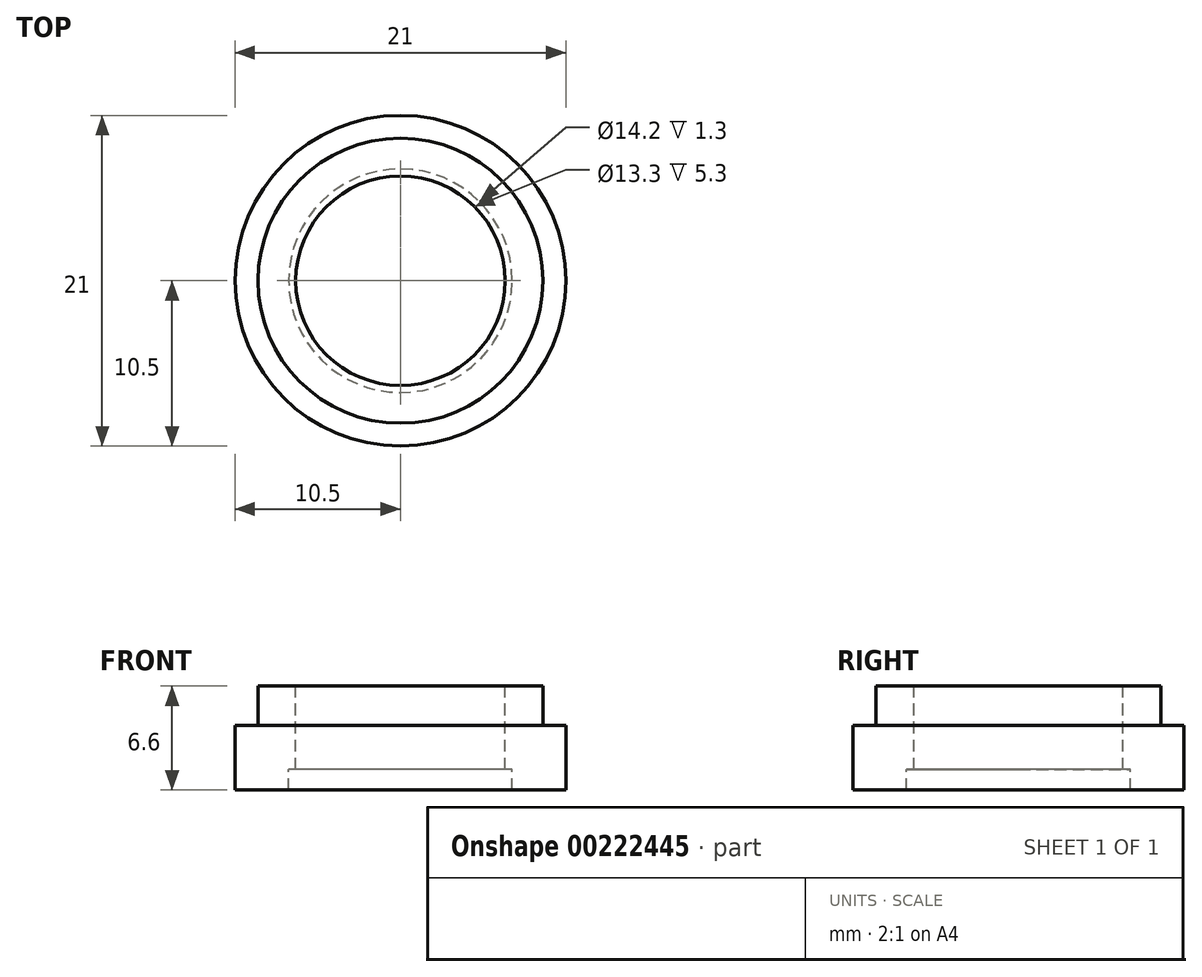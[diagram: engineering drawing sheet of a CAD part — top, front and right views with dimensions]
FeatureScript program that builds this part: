
annotation { "Feature Type Name" : "Feature", "Feature Type Description" : "" }
export const myFeature = defineFeature(function(context is Context, id is Id, definition is map)
    precondition{}
    {
        {
            var Q0;
            Q0=qCreatedBy(makeId("Front.planeOp"),FACE);
            var sketch = newSketch(context, id + "F0", { "sketchPlane" : qUnion([Q0])});
            skLineSegment(sketch, "E0", {"start": v(0, 26.98) * mm, "end": v(0, -14) * mm, "construction": true});
            skLineSegment(sketch, "E1", {"start": v(-7.1, 14.04) * mm, "end": v(-10.5, 14.04) * mm});
            skLineSegment(sketch, "E2", {"start": v(-10.5, 18.14) * mm, "end": v(-9.05, 18.14) * mm});
            skLineSegment(sketch, "E3", {"start": v(-9.05, 18.14) * mm, "end": v(-9.05, 20.64) * mm});
            skLineSegment(sketch, "E4", {"start": v(-9.05, 20.64) * mm, "end": v(-6.65, 20.64) * mm});
            skLineSegment(sketch, "E5", {"start": v(-6.65, 20.64) * mm, "end": v(-6.65, 15.34) * mm});
            skLineSegment(sketch, "E6", {"start": v(-6.65, 15.34) * mm, "end": v(-7.1, 15.34) * mm});
            skLineSegment(sketch, "E7", {"start": v(-7.1, 15.34) * mm, "end": v(-7.1, 14.04) * mm});
            skLineSegment(sketch, "E8", {"start": v(-10.5, 18.14) * mm, "end": v(-10.5, 14.04) * mm});
            skSolve(sketch);
        }
        {
            var Q0;
            Q0 = qSketchRegion(id + "F0", true);
            var Q1;
            Q1=sQuery(id+"F0.wireOp",EDGE,"E0");
            revolve(context, id + "F1", {"entities" : qUnion([Q0]), "axis" : qUnion([Q1]), "revolveType" : RevolveType.FULL});
        }
    });
